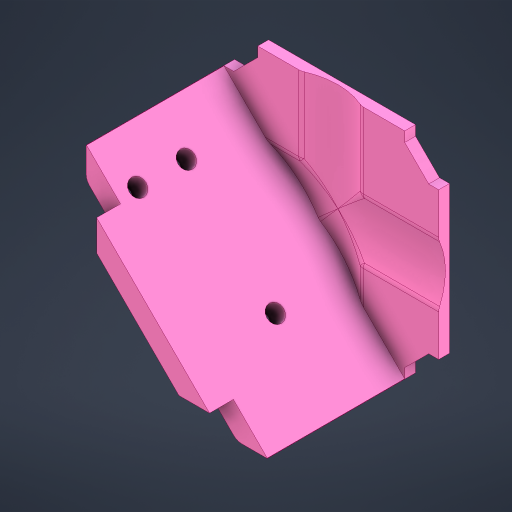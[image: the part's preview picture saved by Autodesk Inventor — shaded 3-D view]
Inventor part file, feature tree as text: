
AUTODESK INVENTOR PART (.ipt)
format: ipt  version: 2023.4 (Build 274418000, 418)  size: 366,080 bytes
history: native  units: mm
features: extrude x9, plane x3, projected_geometry x3, reference x2, other x2, sketch x1, mirror x1, fillet x1
ambient origin geometry x8: Origin, YZ Plane, XZ Plane, XY Plane, X Axis, Y Axis, Z Axis, Center Point
bodies: Solid1 (feature_tree)
feature tree (22):
  plane  "Work Plane1"
  extrude  "Extrusion1"  Depth=2.5mm TaperAngle=0.0deg
  sketch  "Sketch2"  dims[d0=0.075mm d1=2.5mm d2=0.0mm d3=10.0mm d4=10.0mm d5=5.0mm d6=5.0mm d7=2.5mm d8=3.0mm d9=5.0mm d10=31.75mm d11=0.0mm d12=38.75mm d13=22.5mm d14=3.875mm d15=3.875mm d16=3.875mm d17=2.5mm d18=0.0mm d19=2.5mm d20=0.0mm d21=0.75mm d22=5.075mm d23=5.075mm d24=5.075mm d25=1.5mm d26=0.0mm d27=32.5mm d28=1.5mm d29=0.0mm d30=2.5mm d31=0.0mm d32=2.5mm d33=0.0mm d34=2.5mm d35=7.775mm d36=7.775mm d37=0.125mm d38=0.125mm d39=5.5mm d40=0.0mm]
  extrude  "Extrusion2"  Depth=10.0mm
  extrude  "Extrusion3"  Depth=10.0mm
  extrude  "Extrusion4"  Depth=5.0mm
  extrude  "Extrusion5"  Depth=5.0mm
  extrude  "Extrusion6"  Depth=2.5mm
  plane  "Work Plane2"
  extrude  "Extrusion7"  Depth=5.5mm
  plane  "Work Plane3"
  mirror  "Mirror1"
  extrude  "Extrusion8"  Depth=5.0mm
  fillet  "Fillet1"  Radius=31.75mm
  extrude  "Extrusion9"  Depth=5.5mm
  reference  "Reference1"
  projected_geometry  "Projected Loop1"
  projected_geometry  "Projected Loop2"
  projected_geometry  "Projected Loop3"
  reference  "Reference2"
  other  "Cube 1x1 V5.iam"
  other  "Cube 1x1 Bottom V5:1"
